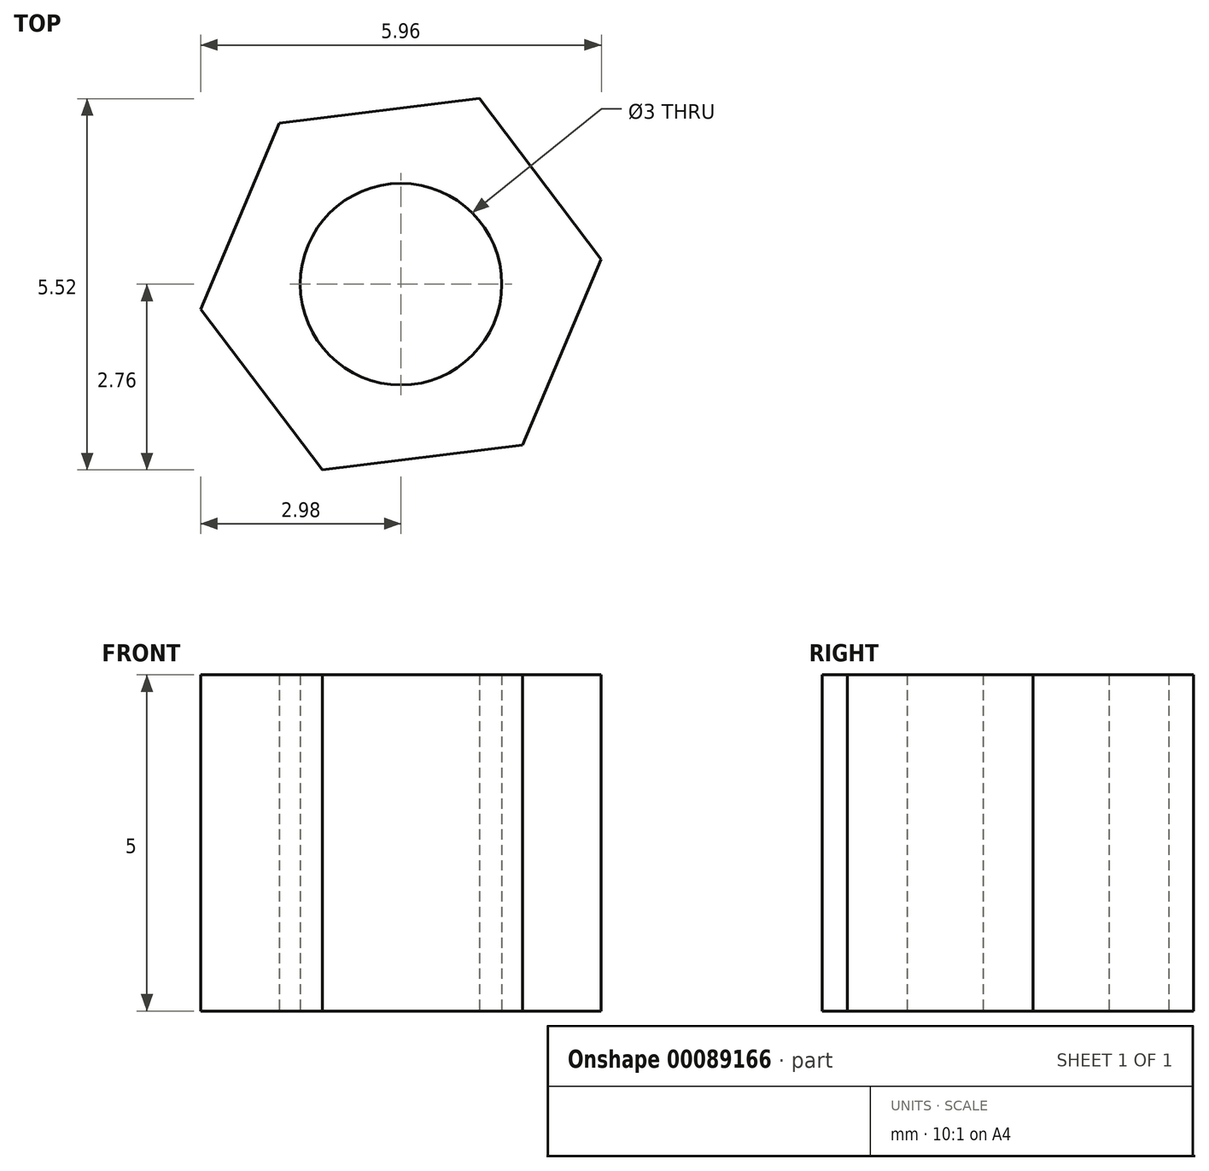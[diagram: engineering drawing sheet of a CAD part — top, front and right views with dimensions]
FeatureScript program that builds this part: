
annotation { "Feature Type Name" : "Feature", "Feature Type Description" : "" }
export const myFeature = defineFeature(function(context is Context, id is Id, definition is map)
    precondition{}
    {
        {
            var Q0;
            Q0=qCreatedBy(makeId("Top.planeOp"),FACE);
            var sketch = newSketch(context, id + "F0", { "sketchPlane" : qUnion([Q0])});
            skCircle(sketch, "E0", {"center": v(0, 0) * mm, "radius": 1.5 * mm});
            skCircle(sketch, "E1.cCircle", {"center": v(0, 0) * mm, "radius": 3 * mm, "construction": true});
            skLineSegment(sketch, "E1.0", {"start": v(-1.8, 2.4) * mm, "end": v(1.17, 2.76) * mm});
            skLineSegment(sketch, "E1.1", {"start": v(1.17, 2.76) * mm, "end": v(2.98, 0.37) * mm});
            skLineSegment(sketch, "E1.2", {"start": v(2.98, 0.37) * mm, "end": v(1.8, -2.4) * mm});
            skLineSegment(sketch, "E1.3", {"start": v(1.8, -2.4) * mm, "end": v(-1.17, -2.76) * mm});
            skLineSegment(sketch, "E1.4", {"start": v(-1.17, -2.76) * mm, "end": v(-2.98, -0.37) * mm});
            skLineSegment(sketch, "E1.5", {"start": v(-2.98, -0.37) * mm, "end": v(-1.8, 2.4) * mm});
            skSolve(sketch);
        }
        {
            var Q0;
            Q0 = qSketchRegion(id + "F0", true);
            extrude(context, id + "F1", {"entities" : qUnion([Q0]), "depth" : 5 * mm});
        }
    });
